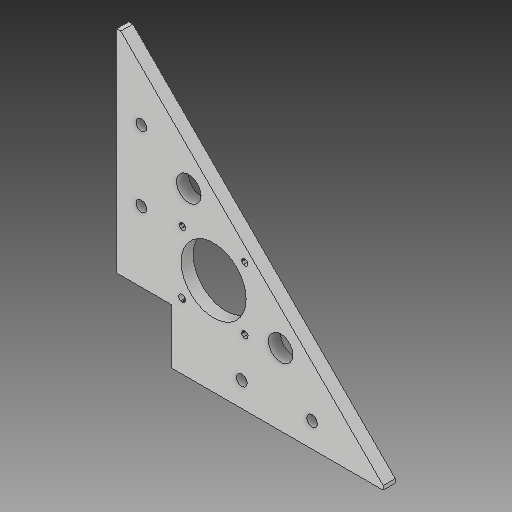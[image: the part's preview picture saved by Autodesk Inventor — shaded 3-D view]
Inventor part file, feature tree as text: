
AUTODESK INVENTOR PART (.ipt)
format: ipt  version: 2017 (Build 210142000, 142)  size: 253,440 bytes
history: native  units: mm
features: other x3, sketch x2
ambient origin geometry x8: Origin, YZ Plane, XZ Plane, XY Plane, X Axis, Y Axis, Z Axis, Center Point
bodies: Solid1 (feature_tree)
feature tree (5):
  other  "Z Motor Mount Right.ipt"
  other  "Solid1::Z Motor Mount Right.ipt"
  other  "TaggingFeature1"
  sketch  "Sketch1"  dims[d0=10.0mm]
  sketch  "Sketch2"
